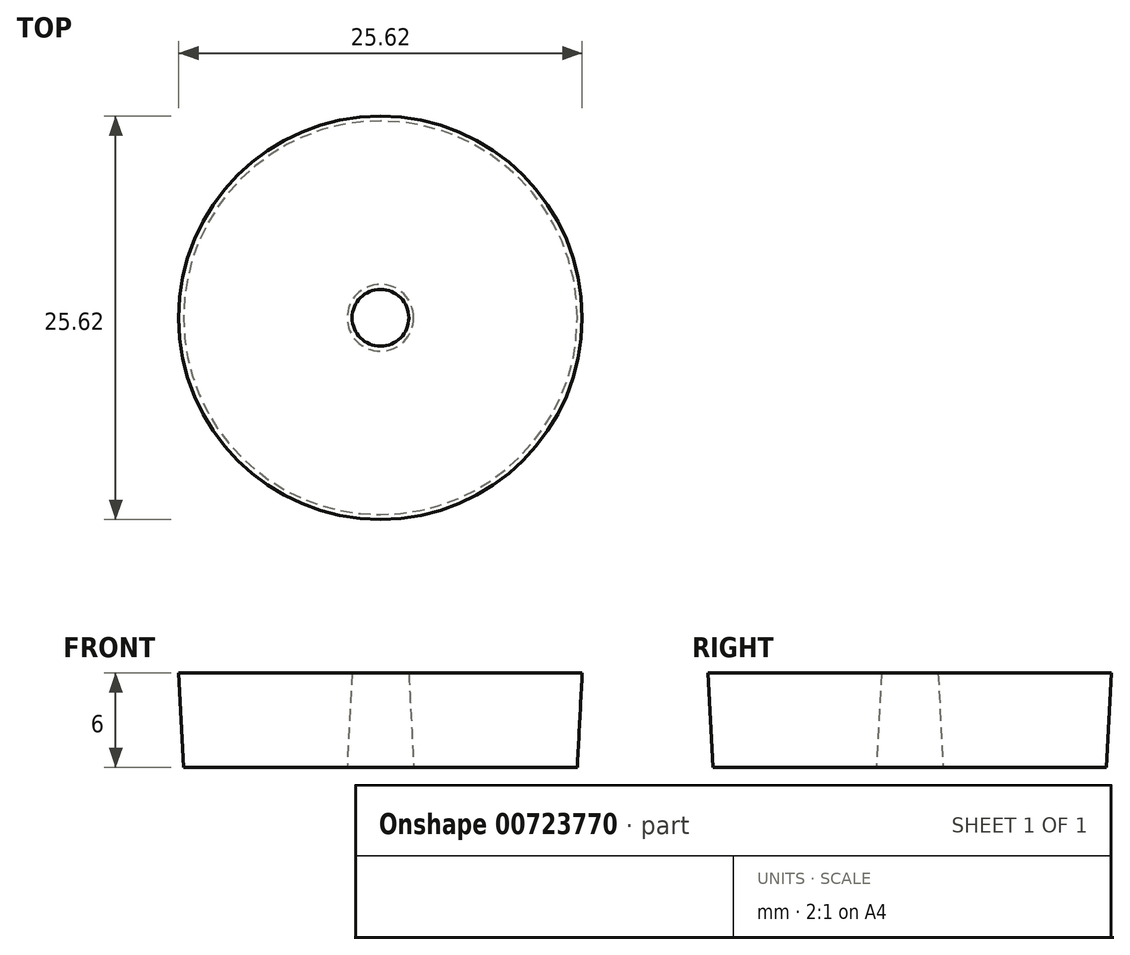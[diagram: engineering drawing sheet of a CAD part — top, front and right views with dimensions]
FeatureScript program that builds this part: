
annotation { "Feature Type Name" : "Feature", "Feature Type Description" : "" }
export const myFeature = defineFeature(function(context is Context, id is Id, definition is map)
    precondition{}
    {
        {
            var Q0;
            Q0=qCreatedBy(makeId("Top.planeOp"),FACE);
            var sketch = newSketch(context, id + "F0", { "sketchPlane" : qUnion([Q0])});
            skCircle(sketch, "E0", {"center": v(0, 0) * mm, "radius": 12.5 * mm});
            skCircle(sketch, "E1", {"center": v(0, 0) * mm, "radius": 2.12 * mm});
            skSolve(sketch);
        }
        {
            var Q0;
            Q0=makeQuery(id+"F0.imprint","IMPRINT",FACE,{"disambiguationData":[TD([[makeQuery(id+"F0.imprint","IMPRINT",EDGE,{"derivedFrom":sQuery(id+"F0.wireOp",EDGE,"E0")}),1.0]])]});
            extrude(context, id + "F1", {"entities" : qUnion([Q0]), "depth" : 6 * mm, "offsetDistance" : 25.4 * mm, "hasDraft" : true, "draftAngle" : 3 * degree});
        }
    });
